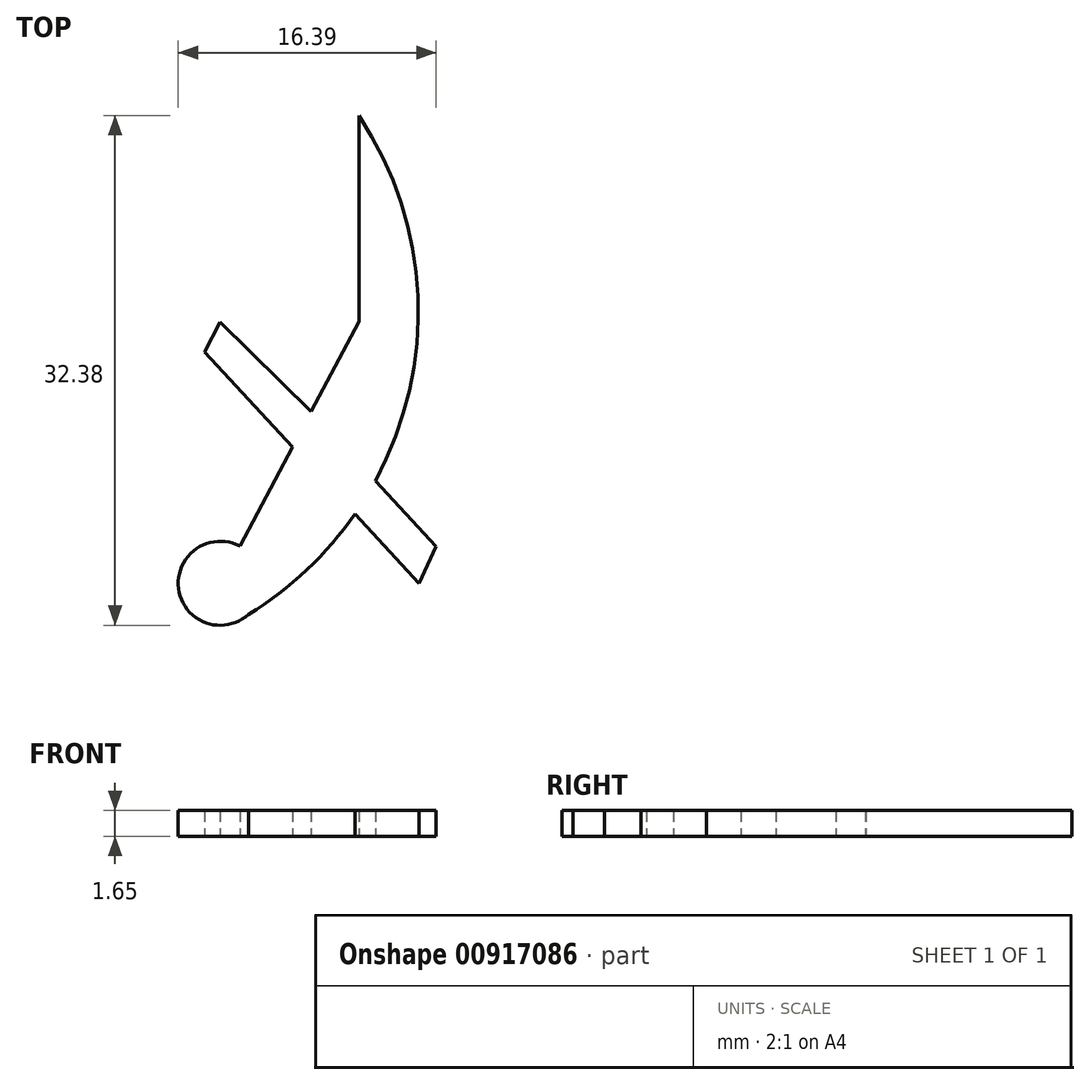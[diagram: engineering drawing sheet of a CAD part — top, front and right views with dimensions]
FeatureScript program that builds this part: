
annotation { "Feature Type Name" : "Feature", "Feature Type Description" : "" }
export const myFeature = defineFeature(function(context is Context, id is Id, definition is map)
    precondition{}
    {
        {
            var Q0;
            Q0=qCreatedBy(makeId("Top.planeOp"),FACE);
            var sketch = newSketch(context, id + "F0", { "sketchPlane" : qUnion([Q0])});
            skArc(sketch, "E0", {"start": v(1.25, 2.36) * mm, "mid": v(-2.65, -0.33) * mm, "end": v(1.8, -1.97) * mm});
            skLineSegment(sketch, "E1", {"start": v(1.25, 2.36) * mm, "end": v(4.6, 8.67) * mm});
            skLineSegment(sketch, "E2", {"start": v(8.8, 16.62) * mm, "end": v(8.8, 29.71) * mm});
            skArc(sketch, "E3", {"start": v(1.8, -1.97) * mm, "mid": v(5.5, 0.86) * mm, "end": v(8.56, 4.4) * mm});
            skLineSegment(sketch, "E4", {"start": v(4.6, 8.67) * mm, "end": v(-1, 14.7) * mm});
            skLineSegment(sketch, "E5", {"start": v(-1, 14.7) * mm, "end": v(0, 16.59) * mm});
            skLineSegment(sketch, "E6", {"start": v(5.78, 10.9) * mm, "end": v(0, 16.59) * mm});
            skLineSegment(sketch, "E7.trimOffspring", {"start": v(5.78, 10.9) * mm, "end": v(8.8, 16.62) * mm});
            skLineSegment(sketch, "E8", {"start": v(8.56, 4.4) * mm, "end": v(12.64, 0) * mm});
            skLineSegment(sketch, "E9", {"start": v(9.85, 6.5) * mm, "end": v(13.72, 2.34) * mm});
            skLineSegment(sketch, "E10", {"start": v(12.64, 0) * mm, "end": v(13.72, 2.34) * mm});
            skArc(sketch, "E11.trimOffspring", {"start": v(9.85, 6.5) * mm, "mid": v(12.55, 18.25) * mm, "end": v(8.8, 29.71) * mm});
            skSolve(sketch);
        }
        {
            var Q0;
            Q0=makeQuery(id+"F0.imprint","IMPRINT",FACE,{"disambiguationData":[TD([[makeQuery(id+"F0.imprint","IMPRINT",EDGE,{"derivedFrom":sQuery(id+"F0.wireOp",EDGE,"E0")}),1.0]])]});
            extrude(context, id + "F1", {"entities" : qUnion([Q0]), "depth" : 1.65 * mm, "offsetDistance" : 25.4 * mm});
        }
    });
